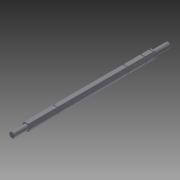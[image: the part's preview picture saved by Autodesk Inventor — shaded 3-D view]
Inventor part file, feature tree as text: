
AUTODESK INVENTOR PART (.ipt)
format: ipt  version: 2014 SP1 (Build 180222100, 222)  size: 164,352 bytes
history: native  units: in
note: dims shown in document units (in); Inventor stores cm internally (conversion verified against a paired STEP export)
features: projected_geometry x5, sketch x3, extrude x2, plane x2, mirror x1, revolve x1
ambient origin geometry x8: Origin, YZ Plane, XZ Plane, XY Plane, X Axis, Y Axis, Z Axis, Center Point
bodies: Solid1 (feature_tree)
feature tree (14):
  extrude  "Extrusion1"  Depth=4.5in TaperAngle=0.0deg
  extrude  "Extrusion2"  Depth=1.0in TaperAngle=0.0deg
  mirror  "Mirror1"
  plane  "Work Plane1"
  revolve  "Revolution1"  [1 undecoded]
  plane  "Work Plane2"
  sketch  "Sketch1"  dims[d0=0.5in d1=4.5in d2=0.0in]
  sketch  "Sketch2"  dims[d3=0.375in d4=1.0in d5=0.0in]
  sketch  "Sketch3"  dims[d6=0.5in d7=0.06in d9=90.0deg d10=0.06in d11=0.22in d13=0.06in d14=0.06in d16=0.563in d18=4.86in d19=2.43in d23=0.063in d24=0.5in d25=0.5in d26=0.01in d27=0.15in]
  projected_geometry  "Projected Loop1"
  projected_geometry  "Projected Loop2"
  projected_geometry  "Projected Loop3"
  projected_geometry  "Projected Loop4"
  projected_geometry  "Projected Loop5"
note: 1 required parameter value undecoded (feature->parameter linkage not recoverable at this tier; creation-order binding heuristic only, values carry confidence <= 0.55)
